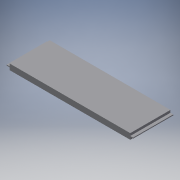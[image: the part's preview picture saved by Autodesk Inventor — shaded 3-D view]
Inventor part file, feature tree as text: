
AUTODESK INVENTOR PART (.ipt)
format: ipt  version: 2018.3 (Build 223284000, 284)  size: 104,448 bytes
history: native  units: mm
features: extrude x3, sketch x3
ambient origin geometry x8: Origin, YZ Plane, XZ Plane, XY Plane, X Axis, Y Axis, Z Axis, Center Point
bodies: Solid1 (feature_tree)
feature tree (6):
  extrude  "Extrusion1"  Depth=14.0mm
  extrude  "Extrusion2"  Depth=0.85mm
  extrude  "Extrusion3"  Depth=1.0mm TaperAngle=0.0deg
  sketch  "Sketch1"  dims[d0=42.0mm d1=14.0mm]
  sketch  "Sketch2"  dims[d2=2.0mm d3=0.0mm d4=0.85mm]
  sketch  "Sketch3"  dims[d5=0.3mm d6=1.0mm d7=0.0mm d8=1.0mm d9=0.0mm]
